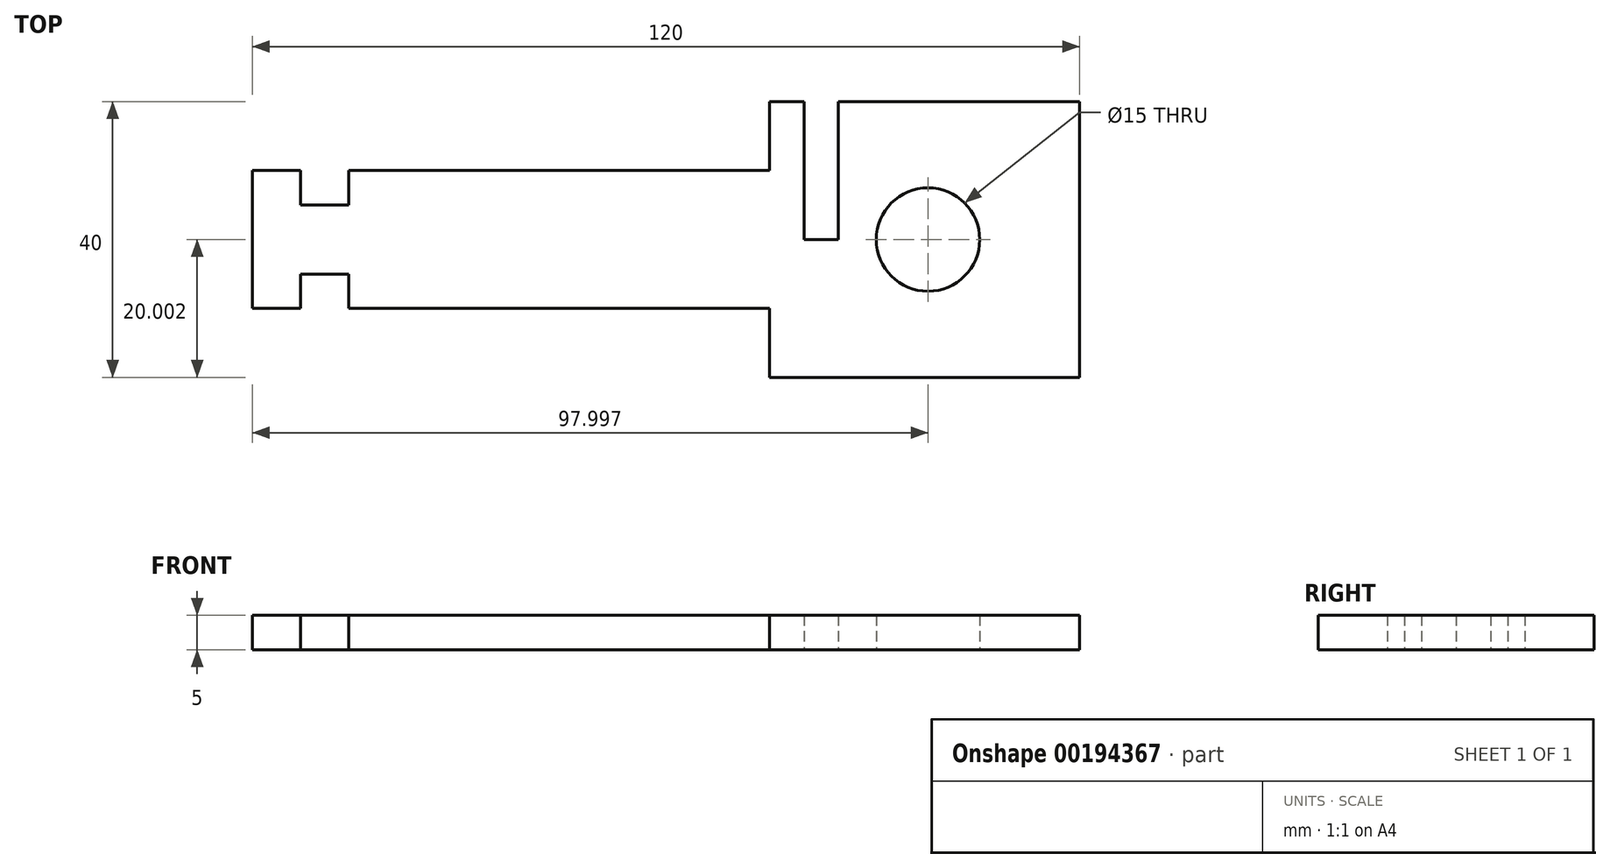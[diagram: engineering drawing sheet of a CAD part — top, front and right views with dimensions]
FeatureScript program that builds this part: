
annotation { "Feature Type Name" : "Feature", "Feature Type Description" : "" }
export const myFeature = defineFeature(function(context is Context, id is Id, definition is map)
    precondition{}
    {
        {
            var Q0;
            Q0=qCreatedBy(makeId("Top.planeOp"),FACE);
            var sketch = newSketch(context, id + "F0", { "sketchPlane" : qUnion([Q0])});
            skLineSegment(sketch, "E0.bottom", {"start": v(-10, 0) * mm, "end": v(10, 0) * mm});
            skLineSegment(sketch, "E0.left", {"start": v(-10, 0) * mm, "end": v(-10, 7) * mm});
            skLineSegment(sketch, "E0.right", {"start": v(10, 0) * mm, "end": v(10, 7) * mm});
            skLineSegment(sketch, "E1.bottom", {"start": v(-20, 120) * mm, "end": v(20, 120) * mm});
            skLineSegment(sketch, "E1.top", {"start": v(-20, 75) * mm, "end": v(-10, 75) * mm});
            skLineSegment(sketch, "E1.left", {"start": v(-20, 120) * mm, "end": v(-20, 115) * mm});
            skLineSegment(sketch, "E1.right", {"start": v(20, 120) * mm, "end": v(20, 75) * mm});
            skPoint(sketch, "E2", {"position": v(0, 75) * mm});
            skLineSegment(sketch, "E3.trimOffspring", {"start": v(10, 75) * mm, "end": v(20, 75) * mm});
            skLineSegment(sketch, "E4", {"start": v(0, 0) * mm, "end": v(0, 75) * mm, "construction": true});
            skLineSegment(sketch, "E5", {"start": v(0, 120) * mm, "end": v(0, 75) * mm, "construction": true});
            skLineSegment(sketch, "E6.bottom", {"start": v(10, 7) * mm, "end": v(5, 7) * mm});
            skLineSegment(sketch, "E6.top", {"start": v(10, 14) * mm, "end": v(5, 14) * mm});
            skLineSegment(sketch, "E6.right", {"start": v(5, 7) * mm, "end": v(5, 14) * mm});
            skLineSegment(sketch, "E7.trimOffspring", {"start": v(10, 14) * mm, "end": v(10, 75) * mm});
            skLineSegment(sketch, "E8.MirrorCS", {"start": v(-10, 14) * mm, "end": v(-5, 14) * mm});
            skLineSegment(sketch, "E9.MirrorCS", {"start": v(-5, 7) * mm, "end": v(-5, 14) * mm});
            skLineSegment(sketch, "E10.MirrorCS", {"start": v(-10, 7) * mm, "end": v(-5, 7) * mm});
            skLineSegment(sketch, "E11.trimOffspring", {"start": v(-10, 14) * mm, "end": v(-10, 75) * mm});
            skLineSegment(sketch, "E12.bottom", {"start": v(-20, 80) * mm, "end": v(0, 80) * mm});
            skLineSegment(sketch, "E12.top", {"start": v(-20, 85) * mm, "end": v(0, 85) * mm});
            skLineSegment(sketch, "E12.right", {"start": v(0, 80) * mm, "end": v(0, 85) * mm});
            skLineSegment(sketch, "E13.trimOffspring", {"start": v(-20, 80) * mm, "end": v(-20, 75) * mm});
            skCircle(sketch, "E14", {"center": v(0, 98) * mm, "radius": 7.5 * mm});
            skLineSegment(sketch, "E15", {"start": v(20, 97.5) * mm, "end": v(-20, 97.5) * mm, "construction": true});
            skLineSegment(sketch, "E16.MirrorCS", {"start": v(-20, 110) * mm, "end": v(0, 110) * mm, "construction": true});
            skLineSegment(sketch, "E17.MirrorCS", {"start": v(0, 115) * mm, "end": v(0, 110) * mm, "construction": true});
            skLineSegment(sketch, "E18.MirrorCS", {"start": v(-20, 115) * mm, "end": v(0, 115) * mm, "construction": true});
            skLineSegment(sketch, "E19.trimOffspring", {"start": v(-20, 110) * mm, "end": v(-20, 85) * mm});
            skLineSegment(sketch, "E20", {"start": v(-20, 115) * mm, "end": v(-20, 110) * mm});
            skSolve(sketch);
        }
        {
            var Q0;
            Q0=qCreatedBy(makeId("Top.planeOp"),FACE);
            var sketch = newSketch(context, id + "F1", { "sketchPlane" : qUnion([Q0])});
            skLineSegment(sketch, "E21.1.0", {"start": v(34.7, -51.21) * mm, "end": v(-40.3, -51.21) * mm, "construction": true});
            skLineSegment(sketch, "E21.1.1", {"start": v(-85.3, -51.21) * mm, "end": v(-40.3, -51.21) * mm, "construction": true});
            skLineSegment(sketch, "E21.1.2", {"start": v(-75.3, -71.21) * mm, "end": v(-50.3, -71.21) * mm, "construction": true});
            skLineSegment(sketch, "E21.1.3", {"start": v(27.7, -46.21) * mm, "end": v(20.7, -46.21) * mm, "construction": true});
            skLineSegment(sketch, "E21.1.4", {"start": v(27.7, -56.21) * mm, "end": v(20.7, -56.21) * mm, "construction": true});
            skLineSegment(sketch, "E21.1.5", {"start": v(34.7, -41.21) * mm, "end": v(27.7, -41.21) * mm, "construction": true});
            skLineSegment(sketch, "E21.1.6", {"start": v(34.7, -61.21) * mm, "end": v(27.7, -61.21) * mm, "construction": true});
            skLineSegment(sketch, "E21.1.7", {"start": v(34.7, -61.21) * mm, "end": v(34.7, -41.21) * mm, "construction": true});
            skLineSegment(sketch, "E21.1.8", {"start": v(-40.3, -71.21) * mm, "end": v(-40.3, -61.21) * mm, "construction": true});
            skLineSegment(sketch, "E21.1.9", {"start": v(-85.3, -71.21) * mm, "end": v(-85.3, -31.21) * mm, "construction": true});
            skLineSegment(sketch, "E21.1.10", {"start": v(-85.3, -31.21) * mm, "end": v(-40.3, -31.21) * mm, "construction": true});
            skCircle(sketch, "E21.1.11", {"center": v(-63.3, -51.21) * mm, "radius": 7.5 * mm, "construction": true});
            skLineSegment(sketch, "E21.1.12", {"start": v(-62.8, -31.21) * mm, "end": v(-62.8, -71.21) * mm, "construction": true});
            skLineSegment(sketch, "E21.1.13", {"start": v(-40.3, -41.21) * mm, "end": v(-40.3, -31.21) * mm, "construction": true});
            skLineSegment(sketch, "E21.1.14", {"start": v(-80.3, -71.21) * mm, "end": v(-80.3, -51.21) * mm, "construction": true});
            skPoint(sketch, "E21.1.15", {"position": v(-40.3, -51.21) * mm});
            skLineSegment(sketch, "E21.1.16", {"start": v(20.7, -61.21) * mm, "end": v(-40.3, -61.21) * mm, "construction": true});
            skLineSegment(sketch, "E21.1.17", {"start": v(20.7, -41.21) * mm, "end": v(-40.3, -41.21) * mm, "construction": true});
            skLineSegment(sketch, "E21.1.18", {"start": v(-45.3, -71.21) * mm, "end": v(-45.3, -51.21) * mm, "construction": true});
            skLineSegment(sketch, "E21.1.19", {"start": v(-75.3, -71.21) * mm, "end": v(-75.3, -51.21) * mm, "construction": true});
            skLineSegment(sketch, "E21.1.20", {"start": v(-50.3, -71.21) * mm, "end": v(-50.3, -51.21) * mm, "construction": true});
            skLineSegment(sketch, "E21.1.21", {"start": v(27.7, -41.21) * mm, "end": v(27.7, -46.21) * mm, "construction": true});
            skLineSegment(sketch, "E21.1.22", {"start": v(20.7, -41.21) * mm, "end": v(20.7, -46.21) * mm, "construction": true});
            skLineSegment(sketch, "E21.1.23", {"start": v(-80.3, -51.21) * mm, "end": v(-75.3, -51.21) * mm, "construction": true});
            skLineSegment(sketch, "E21.1.24", {"start": v(20.7, -61.21) * mm, "end": v(20.7, -56.21) * mm, "construction": true});
            skLineSegment(sketch, "E21.1.25", {"start": v(-85.3, -71.21) * mm, "end": v(-80.3, -71.21) * mm, "construction": true});
            skLineSegment(sketch, "E21.1.26", {"start": v(-45.3, -51.21) * mm, "end": v(-50.3, -51.21) * mm, "construction": true});
            skLineSegment(sketch, "E21.1.27", {"start": v(27.7, -61.21) * mm, "end": v(27.7, -56.21) * mm, "construction": true});
            skLineSegment(sketch, "E21.1.28", {"start": v(-45.3, -71.21) * mm, "end": v(-40.3, -71.21) * mm, "construction": true});
            skLineSegment(sketch, "E21.1.29", {"start": v(-80.3, -71.21) * mm, "end": v(-75.3, -71.21) * mm, "construction": true});
            skLineSegment(sketch, "E21.3.0", {"start": v(-34.7, 51.21) * mm, "end": v(40.3, 51.21) * mm, "construction": true});
            skLineSegment(sketch, "E21.3.1", {"start": v(85.3, 51.21) * mm, "end": v(40.3, 51.21) * mm, "construction": true});
            skLineSegment(sketch, "E21.3.2", {"start": v(75.3, 71.21) * mm, "end": v(50.3, 71.21) * mm});
            skLineSegment(sketch, "E21.3.3", {"start": v(-27.7, 46.21) * mm, "end": v(-20.7, 46.21) * mm});
            skLineSegment(sketch, "E21.3.4", {"start": v(-27.7, 56.21) * mm, "end": v(-20.7, 56.21) * mm});
            skLineSegment(sketch, "E21.3.5", {"start": v(-34.7, 41.21) * mm, "end": v(-27.7, 41.21) * mm});
            skLineSegment(sketch, "E21.3.6", {"start": v(-34.7, 61.21) * mm, "end": v(-27.7, 61.21) * mm});
            skLineSegment(sketch, "E21.3.7", {"start": v(-34.7, 61.21) * mm, "end": v(-34.7, 41.21) * mm});
            skLineSegment(sketch, "E21.3.8", {"start": v(40.3, 71.21) * mm, "end": v(40.3, 61.21) * mm});
            skLineSegment(sketch, "E21.3.9", {"start": v(85.3, 71.21) * mm, "end": v(85.3, 31.21) * mm});
            skLineSegment(sketch, "E21.3.10", {"start": v(85.3, 31.21) * mm, "end": v(40.3, 31.21) * mm});
            skCircle(sketch, "E21.3.11", {"center": v(63.3, 51.21) * mm, "radius": 7.5 * mm});
            skLineSegment(sketch, "E21.3.12", {"start": v(62.8, 31.21) * mm, "end": v(62.8, 71.21) * mm, "construction": true});
            skLineSegment(sketch, "E21.3.13", {"start": v(40.3, 41.21) * mm, "end": v(40.3, 31.21) * mm});
            skLineSegment(sketch, "E21.3.14", {"start": v(80.3, 71.21) * mm, "end": v(80.3, 51.21) * mm, "construction": true});
            skPoint(sketch, "E21.3.15", {"position": v(40.3, 51.21) * mm});
            skLineSegment(sketch, "E21.3.16", {"start": v(-20.7, 61.21) * mm, "end": v(40.3, 61.21) * mm});
            skLineSegment(sketch, "E21.3.17", {"start": v(-20.7, 41.21) * mm, "end": v(40.3, 41.21) * mm});
            skLineSegment(sketch, "E21.3.18", {"start": v(45.3, 71.21) * mm, "end": v(45.3, 51.21) * mm});
            skLineSegment(sketch, "E21.3.19", {"start": v(75.3, 71.21) * mm, "end": v(75.3, 51.21) * mm, "construction": true});
            skLineSegment(sketch, "E21.3.20", {"start": v(50.3, 71.21) * mm, "end": v(50.3, 51.21) * mm});
            skLineSegment(sketch, "E21.3.21", {"start": v(-27.7, 41.21) * mm, "end": v(-27.7, 46.21) * mm});
            skLineSegment(sketch, "E21.3.22", {"start": v(-20.7, 41.21) * mm, "end": v(-20.7, 46.21) * mm});
            skLineSegment(sketch, "E21.3.23", {"start": v(80.3, 51.21) * mm, "end": v(75.3, 51.21) * mm});
            skLineSegment(sketch, "E21.3.24", {"start": v(-20.7, 61.21) * mm, "end": v(-20.7, 56.21) * mm});
            skLineSegment(sketch, "E21.3.25", {"start": v(85.3, 71.21) * mm, "end": v(80.3, 71.21) * mm});
            skLineSegment(sketch, "E21.3.26", {"start": v(45.3, 51.21) * mm, "end": v(50.3, 51.21) * mm});
            skLineSegment(sketch, "E21.3.27", {"start": v(-27.7, 61.21) * mm, "end": v(-27.7, 56.21) * mm});
            skLineSegment(sketch, "E21.3.28", {"start": v(45.3, 71.21) * mm, "end": v(40.3, 71.21) * mm});
            skLineSegment(sketch, "E21.3.29", {"start": v(80.3, 71.21) * mm, "end": v(75.3, 71.21) * mm});
            skPoint(sketch, "E21.center", {"position": v(0, 0) * mm});
            skSolve(sketch);
        }
        {
            var Q0;
            Q0 = qSketchRegion(id + "F1", true);
            extrude(context, id + "F2", {"entities" : qUnion([Q0]), "depth" : 5 * mm});
        }
    });
